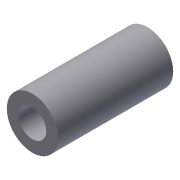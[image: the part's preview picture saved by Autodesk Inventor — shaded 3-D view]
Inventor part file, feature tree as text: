
AUTODESK INVENTOR PART (.ipt)
format: ipt  version: 2011 (Build 150239000, 239)  size: 74,752 bytes
history: native  units: in
note: dims shown in document units (in); Inventor stores cm internally (conversion verified against a paired STEP export)
features: extrude x1, sketch x1
ambient origin geometry x8: Origin, YZ Plane, XZ Plane, XY Plane, X Axis, Y Axis, Z Axis, Center Point
bodies: Solid1 (feature_tree)
feature tree (2):
  extrude  "Extrusion1"  Depth=0.5in
  sketch  "Sketch1"  dims[d0=0.27in d1=0.5in d2=1.125in d3=0.0in]
